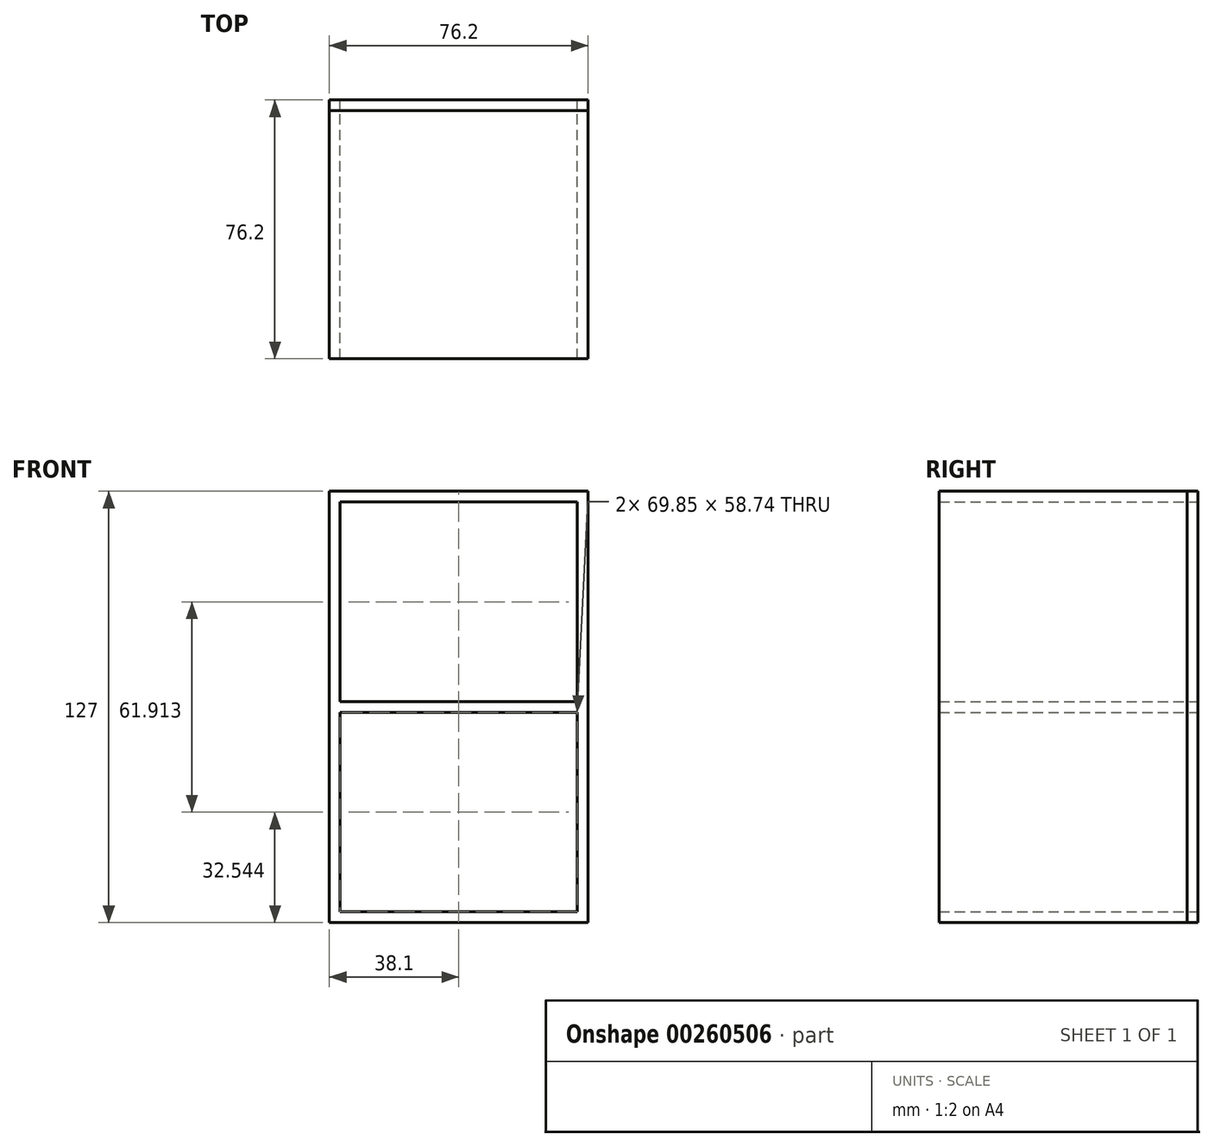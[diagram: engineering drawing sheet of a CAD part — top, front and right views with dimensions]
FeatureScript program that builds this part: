
annotation { "Feature Type Name" : "Feature", "Feature Type Description" : "" }
export const myFeature = defineFeature(function(context is Context, id is Id, definition is map)
    precondition{}
    {
        {
            var Q0;
            Q0=qCreatedBy(makeId("Front.planeOp"),FACE);
            var sketch = newSketch(context, id + "F0", { "sketchPlane" : qUnion([Q0])});
            skLineSegment(sketch, "E0.bottom", {"start": v(-38.1, -63.5) * mm, "end": v(38.1, -63.5) * mm});
            skLineSegment(sketch, "E0.top", {"start": v(-38.1, 63.5) * mm, "end": v(38.1, 63.5) * mm});
            skLineSegment(sketch, "E0.left", {"start": v(-38.1, -63.5) * mm, "end": v(-38.1, 63.5) * mm});
            skLineSegment(sketch, "E0.right", {"start": v(38.1, -63.5) * mm, "end": v(38.1, 63.5) * mm});
            skPoint(sketch, "E0.middle", {"position": v(0, 0) * mm});
            skLineSegment(sketch, "E1.bottom", {"start": v(-34.92, -60.33) * mm, "end": v(34.93, -60.33) * mm});
            skLineSegment(sketch, "E1.top", {"start": v(-34.93, 60.33) * mm, "end": v(34.93, 60.33) * mm});
            skLineSegment(sketch, "E1.left", {"start": v(-34.92, -60.33) * mm, "end": v(-34.93, 60.33) * mm});
            skLineSegment(sketch, "E1.right", {"start": v(34.93, -60.33) * mm, "end": v(34.92, 60.33) * mm});
            skLineSegment(sketch, "E2", {"start": v(-34.92, -1.59) * mm, "end": v(34.92, -1.59) * mm});
            skLineSegment(sketch, "E3", {"start": v(-34.93, 1.59) * mm, "end": v(34.92, 1.59) * mm});
            skPoint(sketch, "E4", {"position": v(-34.93, 0) * mm});
            skPoint(sketch, "E5", {"position": v(34.93, 0) * mm});
            skSolve(sketch);
        }
        {
            var Q0;
            Q0 = qSketchRegion(id + "F0", true);
            var Q1;
            {var subQ0=sQuery(id+"F0.wireOp",EDGE,"E2");Q1=makeQuery(id+"F0.imprint","IMPRINT",FACE,{"disambiguationData":[TD([[makeQuery(id+"F0.imprint","IMPRINT",EDGE,{"derivedFrom":subQ0}),1.0]])]});}
            var Q2;
            {var subQ0=sQuery(id+"F0.wireOp",EDGE,"E1.top");Q2=makeQuery(id+"F0.imprint","IMPRINT",FACE,{"disambiguationData":[TD([[makeQuery(id+"F0.imprint","IMPRINT",EDGE,{"derivedFrom":subQ0}),-1.0]])]});}
            var Q3;
            {var subQ0=sQuery(id+"F0.wireOp",EDGE,"E1.bottom");Q3=makeQuery(id+"F0.imprint","IMPRINT",FACE,{"disambiguationData":[TD([[makeQuery(id+"F0.imprint","IMPRINT",EDGE,{"derivedFrom":subQ0}),1.0]])]});}
            extrude(context, id + "F1", {"entities" : qUnion([Q0, Q1, Q2, Q3]), "depth" : 3.17 * mm});
        }
        {
            var Q0;
            Q0 = qSketchRegion(id + "F0", true);
            var Q1;
            {var subQ0=sQuery(id+"F0.wireOp",EDGE,"E2");Q1=makeQuery(id+"F0.imprint","IMPRINT",FACE,{"disambiguationData":[TD([[makeQuery(id+"F0.imprint","IMPRINT",EDGE,{"derivedFrom":subQ0}),1.0]])]});}
            extrude(context, id + "F2", {"entities" : qUnion([Q0, Q1]), "depth" : 76.2 * mm});
        }
    });
